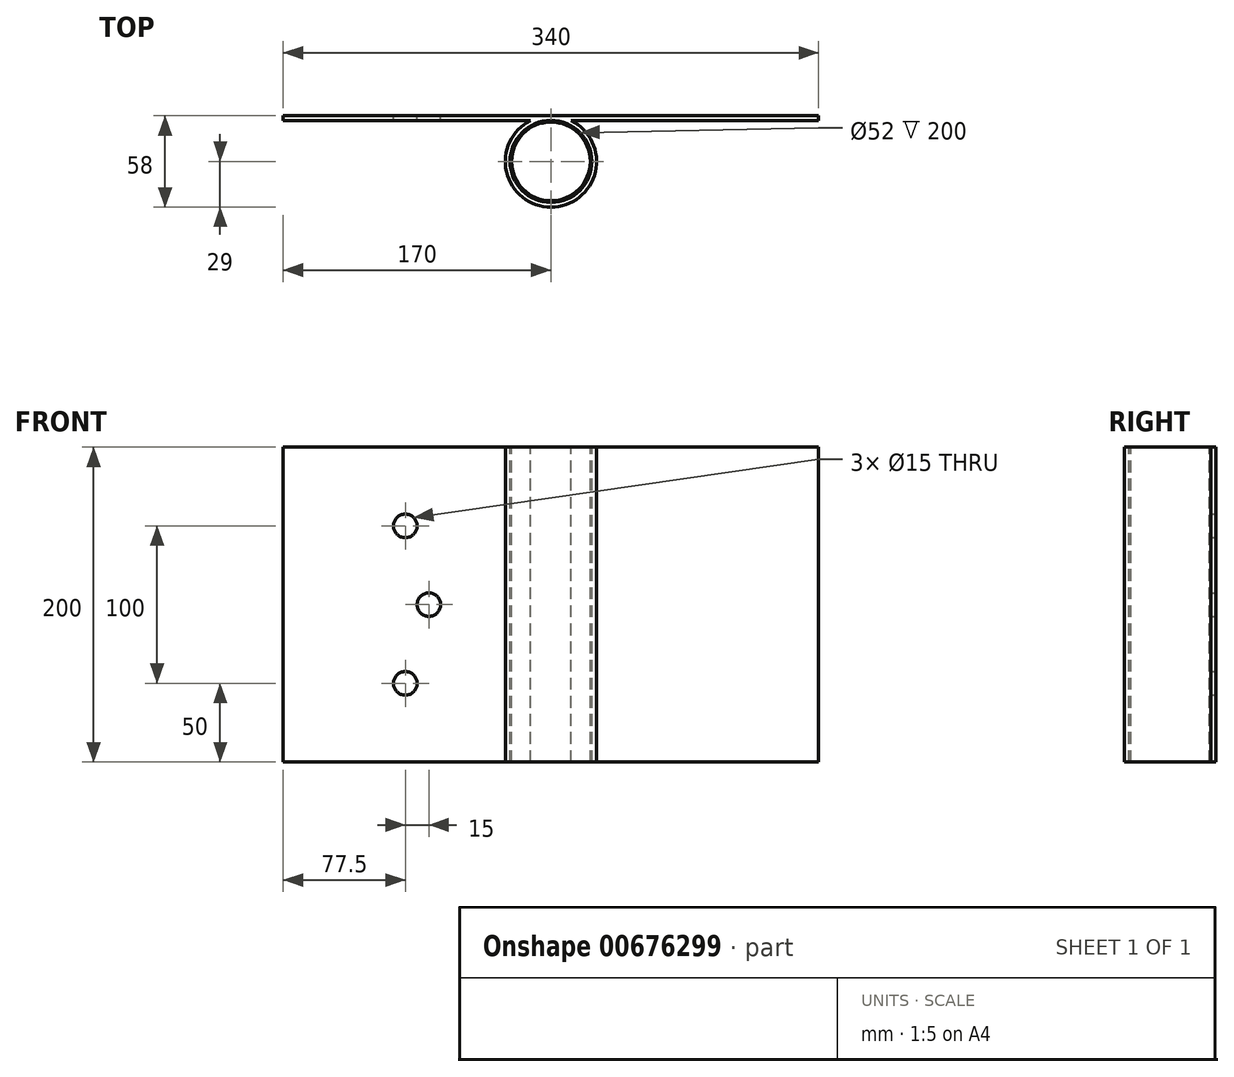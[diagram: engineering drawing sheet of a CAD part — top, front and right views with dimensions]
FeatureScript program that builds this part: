
annotation { "Feature Type Name" : "Feature", "Feature Type Description" : "" }
export const myFeature = defineFeature(function(context is Context, id is Id, definition is map)
    precondition{}
    {
        {
            assignVariable(context, id + "F0", {"name" : "PinL", "anyValue" : 200});
        }
        {
            var Q0;
            Q0=qCreatedBy(makeId("Front.planeOp"),FACE);
            var sketch = newSketch(context, id + "F1", { "sketchPlane" : qUnion([Q0])});
            skLineSegment(sketch, "E0.bottom", {"start": v(0, 100) * mm, "end": v(-25, 100) * mm});
            skLineSegment(sketch, "E0.top", {"start": v(0, -100) * mm, "end": v(-25, -100) * mm});
            skLineSegment(sketch, "E0.left", {"start": v(0, 100) * mm, "end": v(0, -100) * mm});
            skLineSegment(sketch, "E0.right", {"start": v(-25, 100) * mm, "end": v(-25, -100) * mm});
            skSolve(sketch);
        }
        {
            var Q0;
            Q0=makeQuery(id+"F1.imprint","IMPRINT",FACE,{"disambiguationData":[TD([[makeQuery(id+"F1.imprint","IMPRINT",EDGE,{"derivedFrom":sQuery(id+"F1.wireOp",EDGE,"E0.bottom")}),1.0]])]});
            var Q1;
            Q1=sQuery(id+"F1.wireOp",EDGE,"E0.left");
            revolve(context, id + "F2", {"entities" : qUnion([Q0]), "axis" : qUnion([Q1]), "revolveType" : RevolveType.FULL});
        }
        {
            var Q0;
            Q0=makeQuery(id+"F2.opRevolve","SWEPT_FACE",FACE,{"disambiguationData":[OSD([sQuery(id+"F1.wireOp",EDGE,"E0.bottom")])]});
            var sketch = newSketch(context, id + "F3", { "sketchPlane" : qUnion([Q0])});
            skCircle(sketch, "E1.0", {"center": v(0, 0) * mm, "radius": 25 * mm, "construction": true});
            skCircle(sketch, "E2", {"center": v(0, 0) * mm, "radius": 26 * mm});
            skCircle(sketch, "E3", {"center": v(0, 0) * mm, "radius": 29 * mm});
            skSolve(sketch);
        }
        {
            var Q0;
            Q0 = qSketchRegion(id + "F3", true);
            extrude(context, id + "F4", {"entities" : qUnion([Q0]), "oppositeDirection" : true, "depth" : (getVariable(context, 'PinL') / 3) * mm, "offsetDistance" : 25 * mm});
        }
        {
            var Q0;
            Q0 = qSketchRegion(id + "F3", true);
            extrude(context, id + "F5", {"entities" : qUnion([Q0]), "oppositeDirection" : true, "depth" : (getVariable(context, 'PinL')) * mm, "offsetDistance" : 25 * mm, "hasSecondDirection" : true, "secondDirectionOppositeDirection" : true, "secondDirectionDepth" : (getVariable(context, 'PinL') * .66666) * mm});
        }
        {
            var Q0;
            Q0 = qSketchRegion(id + "F3", true);
            extrude(context, id + "F6", {"entities" : qUnion([Q0]), "oppositeDirection" : true, "depth" : (getVariable(context, 'PinL') * 2 / 3) * mm, "offsetDistance" : 25 * mm, "hasSecondDirection" : true, "secondDirectionOppositeDirection" : true, "secondDirectionDepth" : (getVariable(context, 'PinL') / 3) * mm});
        }
        {
            var Q0;
            Q0=makeQuery(id+"F4.opExtrude","CAP_FACE",FACE,{"disambiguationData":[OSD([sQuery(id+"F3.wireOp",EDGE,"E2"),sQuery(id+"F3.wireOp",EDGE,"E3")])],"isStart":true});
            var sketch = newSketch(context, id + "F7", { "sketchPlane" : qUnion([Q0])});
            skLineSegment(sketch, "E4", {"start": v(0, 29) * mm, "end": v(170, 29) * mm});
            skLineSegment(sketch, "E5", {"start": v(170, 29) * mm, "end": v(170, 26) * mm});
            skLineSegment(sketch, "E6", {"start": v(170, 26) * mm, "end": v(0, 26) * mm});
            skLineSegment(sketch, "E7", {"start": v(0, 26) * mm, "end": v(0, 29) * mm});
            skSolve(sketch);
        }
        {
            var Q0;
            Q0 = qSketchRegion(id + "F7", true);
            extrude(context, id + "F8", {"entities" : qUnion([Q0]), "operationType" : NewBodyOperationType.ADD, "oppositeDirection" : true, "depth" : (getVariable(context, 'PinL')) * mm, "offsetDistance" : 25 * mm});
        }
        {
            var Q0;
            Q0=makeQuery(id+"F8.boolean.opBoolean","MERGE",FACE,{"derivedFrom":[makeQuery(id+"F4.opExtrude","CAP_FACE",FACE,{"disambiguationData":[OSD([sQuery(id+"F3.wireOp",EDGE,"E2"),sQuery(id+"F3.wireOp",EDGE,"E3")])],"isStart":true}),makeQuery(id+"F8.opExtrude","CAP_FACE",FACE,{"disambiguationData":[OSD([sQuery(id+"F7.wireOp",EDGE,"E4"),sQuery(id+"F7.wireOp",EDGE,"E5"),sQuery(id+"F7.wireOp",EDGE,"E6"),sQuery(id+"F7.wireOp",EDGE,"E7")])],"isStart":true})]});
            var sketch = newSketch(context, id + "F9", { "sketchPlane" : qUnion([Q0])});
            skLineSegment(sketch, "E8.0", {"start": v(0, 26) * mm, "end": v(0, 29) * mm});
            skLineSegment(sketch, "E9", {"start": v(0, 29) * mm, "end": v(-170, 29) * mm});
            skLineSegment(sketch, "E10", {"start": v(-170, 29) * mm, "end": v(-170, 26) * mm});
            skLineSegment(sketch, "E11", {"start": v(-170, 26) * mm, "end": v(0, 26) * mm});
            skSolve(sketch);
        }
        {
            var Q0;
            Q0 = qSketchRegion(id + "F9", true);
            extrude(context, id + "F10", {"entities" : qUnion([Q0]), "operationType" : NewBodyOperationType.ADD, "oppositeDirection" : true, "depth" : (getVariable(context, 'PinL')) * mm, "offsetDistance" : 25 * mm});
        }
        {
            var Q0;
            Q0=makeQuery(id+"F10.opExtrude","SWEPT_FACE",FACE,{"disambiguationData":[OSD([sQuery(id+"F9.wireOp",EDGE,"E9")])]});
            var sketch = newSketch(context, id + "F11", { "sketchPlane" : qUnion([Q0])});
            skCircle(sketch, "E12", {"center": v(77.5, 0) * mm, "radius": 7.5 * mm});
            skCircle(sketch, "E13", {"center": v(92.5, 50) * mm, "radius": 7.5 * mm});
            skCircle(sketch, "E14", {"center": v(92.5, -50) * mm, "radius": 7.5 * mm});
            skLineSegment(sketch, "E15", {"start": v(85, 100) * mm, "end": v(85, -100) * mm, "construction": true});
            skLineSegment(sketch, "E16", {"start": v(-77.09, 0) * mm, "end": v(101.8, 0) * mm, "construction": true});
            skPoint(sketch, "E17", {"position": v(85, 0) * mm});
            skSolve(sketch);
        }
        {
            var Q0;
            Q0 = qSketchRegion(id + "F11", true);
            extrude(context, id + "F12", {"entities" : qUnion([Q0]), "operationType" : NewBodyOperationType.REMOVE, "oppositeDirection" : true, "depth" : 25 * mm, "offsetDistance" : 25 * mm});
        }
    });
